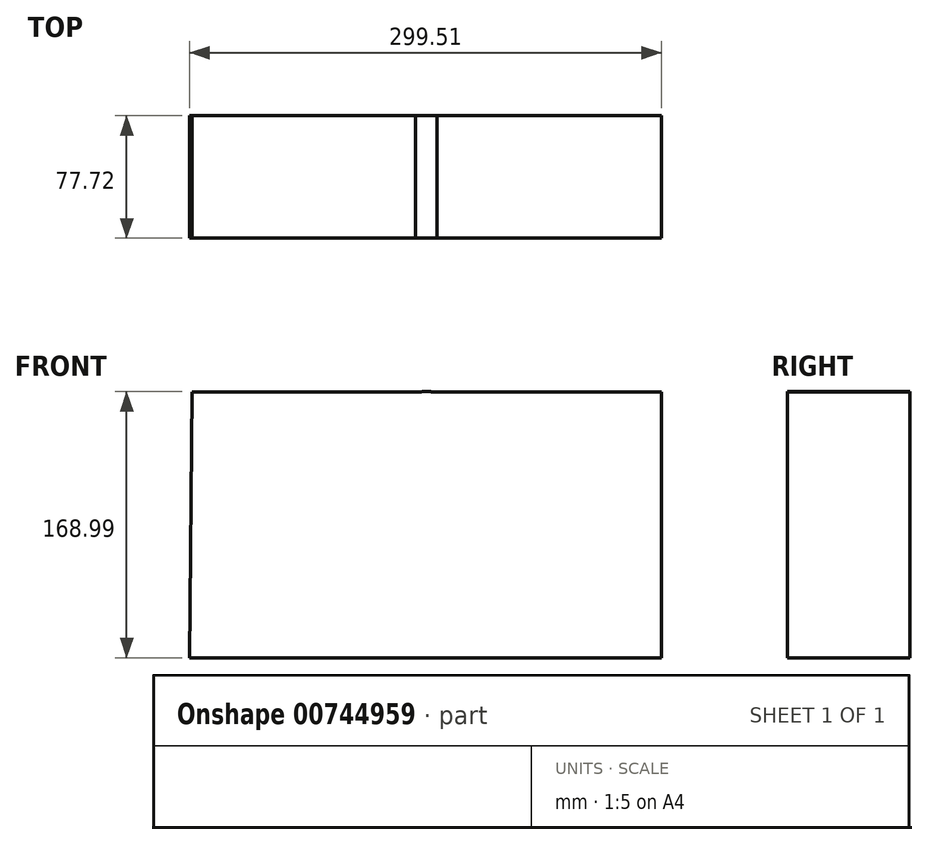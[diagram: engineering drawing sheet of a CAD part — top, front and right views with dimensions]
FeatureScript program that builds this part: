
annotation { "Feature Type Name" : "Feature", "Feature Type Description" : "" }
export const myFeature = defineFeature(function(context is Context, id is Id, definition is map)
    precondition{}
    {
        {
            var Q0;
            Q0=qCreatedBy(makeId("Front.planeOp"),FACE);
            var sketch = newSketch(context, id + "F0", { "sketchPlane" : qUnion([Q0])});
            skLineSegment(sketch, "E0", {"start": v(-148.7, 83.9) * mm, "end": v(149.26, 83.9) * mm});
            skLineSegment(sketch, "E1", {"start": v(149.26, 83.9) * mm, "end": v(149.26, -84.82) * mm});
            skLineSegment(sketch, "E2", {"start": v(149.26, -84.82) * mm, "end": v(-150.25, -84.82) * mm});
            skLineSegment(sketch, "E3", {"start": v(-148.7, 83.9) * mm, "end": v(-150.25, -84.82) * mm});
            skCircle(sketch, "E4", {"center": v(0, 0) * mm, "radius": 84.17 * mm});
            skSolve(sketch);
        }
        {
            var Q0;
            Q0 = qSketchRegion(id + "F0", true);
            extrude(context, id + "F1", {"entities" : qUnion([Q0]), "depth" : 77.72 * mm, "offsetDistance" : 25.4 * mm});
        }
    });
